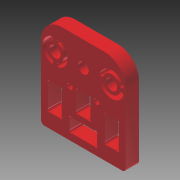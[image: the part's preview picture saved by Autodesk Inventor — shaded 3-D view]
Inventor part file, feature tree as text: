
AUTODESK INVENTOR PART (.ipt)
format: ipt  version: 2012 SP1 (Build 160190100, 190)  size: 228,864 bytes
history: native  units: in
note: dims shown in document units (in); Inventor stores cm internally (conversion verified against a paired STEP export)
features: other x4, extrude x2
ambient origin geometry x8: Origin, YZ Plane, XZ Plane, XY Plane, X Axis, Y Axis, Z Axis, Center Point
bodies: Solid1 (feature_tree)
feature tree (6):
  other  "skeleton.ipt"
  other  "POCKET_1-4"
  other  "STOCK_12MM"
  extrude  "Extrusion1"  Depth=0.3937in
  extrude  "Extrusion2"  Depth=0.4724in
  other  "THROUGH-CUT"
